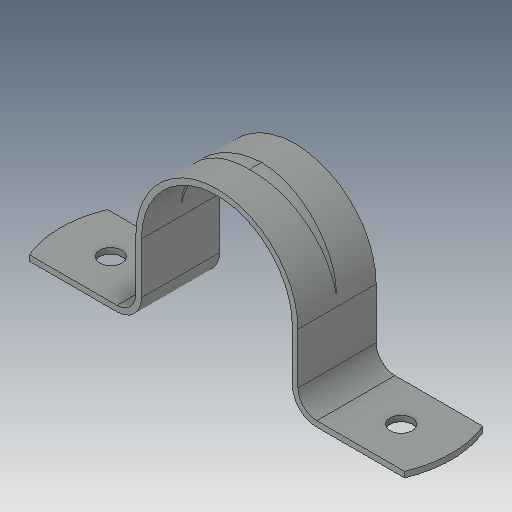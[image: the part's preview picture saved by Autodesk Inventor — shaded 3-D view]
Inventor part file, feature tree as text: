
AUTODESK INVENTOR PART (.ipt)
format: ipt  version: 2023.5 (Build 275446000, 446)  size: 167,936 bytes
history: native  units: in
note: dims shown in document units (in); Inventor stores cm internally (conversion verified against a paired STEP export)
features: mirror x1
ambient origin geometry x8: Origin, YZ Plane, XZ Plane, XY Plane, X Axis, Y Axis, Z Axis, Center Point
bodies: Solid1 (feature_tree)
feature tree (1):
  mirror  "Mirror1"
